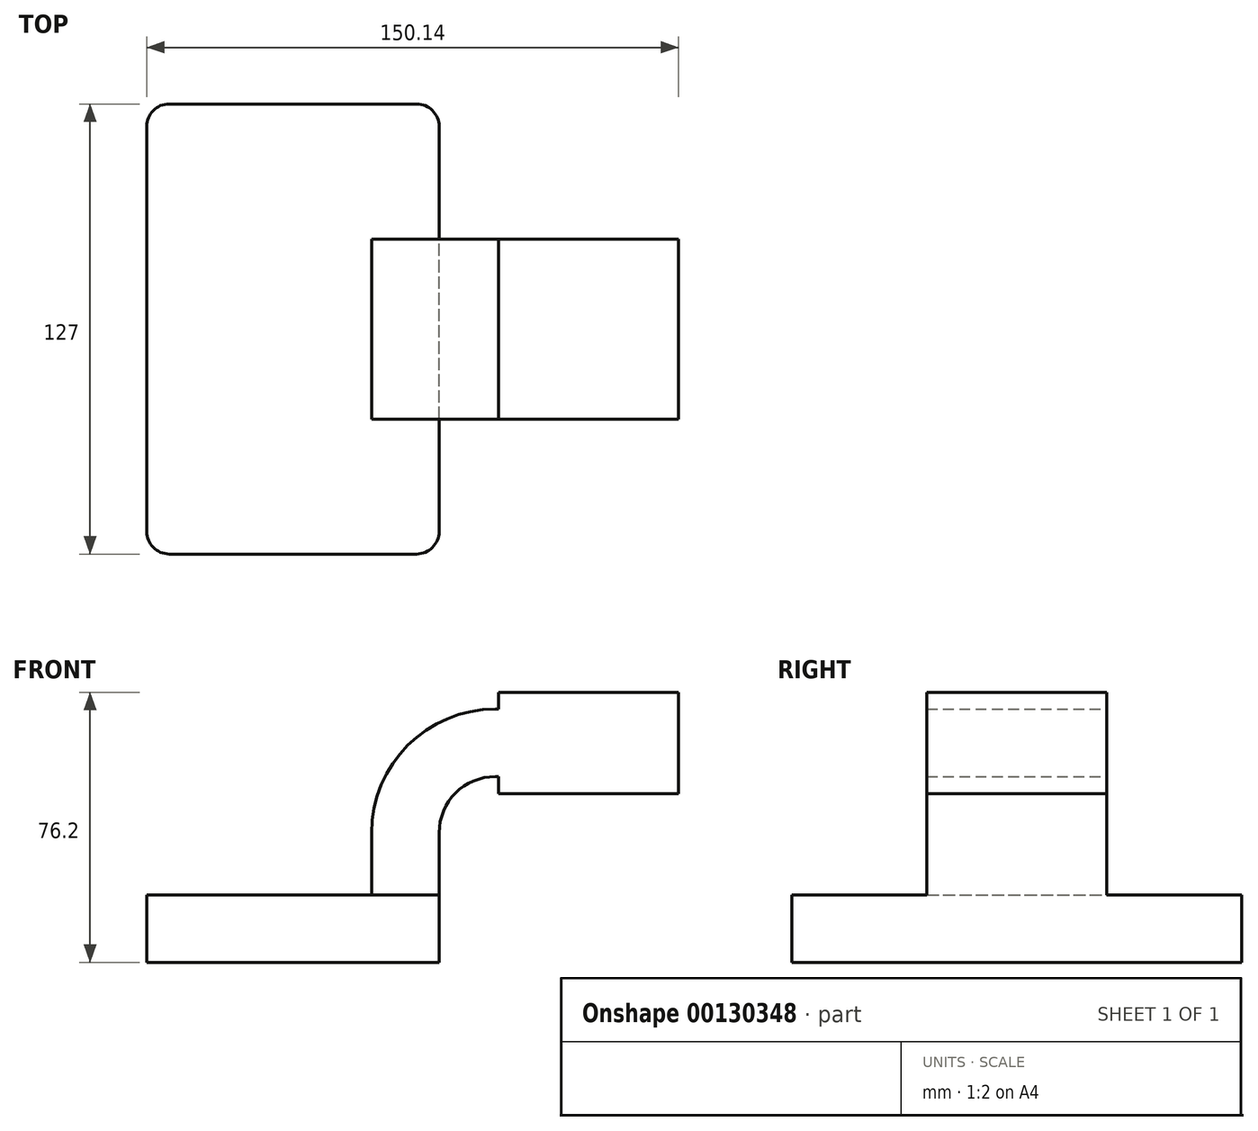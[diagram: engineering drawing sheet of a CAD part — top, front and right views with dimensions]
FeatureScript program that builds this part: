
annotation { "Feature Type Name" : "Feature", "Feature Type Description" : "" }
export const myFeature = defineFeature(function(context is Context, id is Id, definition is map)
    precondition{}
    {
        {
            var Q0;
            Q0=qCreatedBy(makeId("Front.planeOp"),FACE);
            var sketch = newSketch(context, id + "F0", { "sketchPlane" : qUnion([Q0])});
            skLineSegment(sketch, "E0.bottom", {"start": v(41.28, -9.52) * mm, "end": v(-41.28, -9.53) * mm});
            skLineSegment(sketch, "E0.top", {"start": v(41.28, 9.53) * mm, "end": v(-41.28, 9.53) * mm});
            skLineSegment(sketch, "E0.left", {"start": v(41.28, -9.52) * mm, "end": v(41.28, 9.53) * mm});
            skLineSegment(sketch, "E0.right", {"start": v(-41.28, -9.53) * mm, "end": v(-41.28, 9.53) * mm});
            skPoint(sketch, "E0.middle", {"position": v(0, 0) * mm});
            skLineSegment(sketch, "E1.bottom", {"start": v(108.87, 38.1) * mm, "end": v(58.07, 38.1) * mm});
            skLineSegment(sketch, "E1.top", {"start": v(108.87, 66.68) * mm, "end": v(58.07, 66.68) * mm});
            skLineSegment(sketch, "E1.left", {"start": v(108.87, 38.1) * mm, "end": v(108.87, 66.68) * mm});
            skLineSegment(sketch, "E1.right", {"start": v(58.07, 38.1) * mm, "end": v(58.07, 66.68) * mm});
            skPoint(sketch, "E1.middle", {"position": v(83.47, 52.39) * mm});
            skLineSegment(sketch, "E2", {"start": v(41.28, 9.53) * mm, "end": v(41.28, 27) * mm});
            skArc(sketch, "E3", {"start": v(41.27, 27) * mm, "mid": v(45.92, 38.23) * mm, "end": v(57.15, 42.88) * mm});
            skLineSegment(sketch, "E4", {"start": v(57.15, 42.88) * mm, "end": v(85.72, 42.88) * mm});
            skLineSegment(sketch, "E5.0", {"start": v(57.15, 61.93) * mm, "end": v(85.72, 61.93) * mm});
            skArc(sketch, "E5.1", {"start": v(22.23, 27) * mm, "mid": v(32.45, 51.7) * mm, "end": v(57.15, 61.93) * mm});
            skLineSegment(sketch, "E5.2", {"start": v(22.23, 9.53) * mm, "end": v(22.23, 27) * mm});
            skLineSegment(sketch, "E6", {"start": v(85.72, 42.88) * mm, "end": v(85.72, 66.68) * mm});
            skLineSegment(sketch, "E7", {"start": v(85.72, 42.88) * mm, "end": v(85.72, 38.1) * mm});
            skPoint(sketch, "E7.endSnap0", {"position": v(83.47, 38.1) * mm});
            skFitSpline(sketch, "E8", {"points": [v(-41.28, 9.53) * mm, v(57.15, 61.93) * mm], "startDerivative": vector(-1.56, 64.84) * mm, "endDerivative": vector(113.57, -0.62) * mm});
            skSolve(sketch);
        }
        {
            var Q0;
            Q0=makeQuery(id+"F0.imprint","IMPRINT",FACE,{"disambiguationData":[TD([[makeQuery(id+"F0.imprint","IMPRINT",EDGE,{"derivedFrom":sQuery(id+"F0.wireOp",EDGE,"E0.bottom")}),-1.0]])]});
            extrude(context, id + "F1", {"entities" : qUnion([Q0]), "endBound" : BoundingType.SYMMETRIC, "depth" : 127 * mm});
        }
        {
            var Q0;
            {var subQ1=sQuery(id+"F0.wireOp",EDGE,"E2");Q0=makeQuery(id+"F0.imprint","IMPRINT",FACE,{"disambiguationData":[TD([[makeQuery(id+"F0.imprint","IMPRINT",EDGE,{"derivedFrom":subQ1}),1.0]])]});}
            var Q1;
            {var subQ0=sQuery(id+"F0.wireOp",EDGE,"E4");var subQ1=sQuery(id+"F0.wireOp",EDGE,"E1.right");var subQ2=makeQuery(id+"F0.imprint","INTERSECT",VERTEX,{"derivedFrom":[subQ1,subQ0]});Q1=makeQuery(id+"F0.imprint","IMPRINT",FACE,{"disambiguationData":[TD([[makeQuery(id+"F0.imprint","IMPRINT",EDGE,{"disambiguationData":[TD([[subQ2,-1.0]])],"derivedFrom":subQ1}),-1.0]])]});}
            var Q2;
            {var subQ0=sQuery(id+"F0.wireOp",EDGE,"E1.left");Q2=makeQuery(id+"F0.imprint","IMPRINT",FACE,{"disambiguationData":[TD([[makeQuery(id+"F0.imprint","IMPRINT",EDGE,{"derivedFrom":subQ0}),1.0]])]});}
            var Q3;
            {var subQ0=sQuery(id+"F0.wireOp",EDGE,"E1.right");var subQ1=sQuery(id+"F0.wireOp",EDGE,"E1.top");var subQ2=makeQuery(id+"F0.imprint","INTERSECT",VERTEX,{"derivedFrom":[subQ1,subQ0]});Q3=makeQuery(id+"F0.imprint","IMPRINT",FACE,{"disambiguationData":[TD([[makeQuery(id+"F0.imprint","IMPRINT",EDGE,{"disambiguationData":[TD([[subQ2,1.0]])],"derivedFrom":subQ1}),1.0]])]});}
            var Q4;
            {var subQ3=sQuery(id+"F0.wireOp",EDGE,"E7");Q4=makeQuery(id+"F0.imprint","IMPRINT",FACE,{"disambiguationData":[TD([[makeQuery(id+"F0.imprint","IMPRINT",EDGE,{"derivedFrom":subQ3}),-1.0]])]});}
            extrude(context, id + "F2", {"entities" : qUnion([Q0, Q1, Q2, Q3, Q4]), "operationType" : NewBodyOperationType.ADD, "endBound" : BoundingType.SYMMETRIC, "depth" : 50.8 * mm});
        }
        {
            var Q0;
            Q0=makeQuery(id+"F0.imprint","IMPRINT",FACE,{"disambiguationData":[TD([[makeQuery(id+"F0.imprint","IMPRINT",EDGE,{"derivedFrom":sQuery(id+"F0.wireOp",EDGE,"E5.1")}),1.0]])]});
            extrude(context, id + "F3", {"entities" : qUnion([Q0]), "operationType" : NewBodyOperationType.ADD, "depth" : 19.05 * mm});
        }
        {
            var Q0;
            Q0=makeQuery(id+"F1.opExtrude","CAP_EDGE",EDGE,{"disambiguationData":[OSD([sQuery(id+"F0.wireOp",EDGE,"E0.left")])],"isStart":false});
            var Q1;
            Q1=makeQuery(id+"F1.opExtrude","CAP_EDGE",EDGE,{"disambiguationData":[OSD([sQuery(id+"F0.wireOp",EDGE,"E0.right")])],"isStart":false});
            fillet(context, id + "F4", {"entities" : qUnion([Q0, Q1]), "radius" : 6.35 * mm, "tangentPropagation" : true, "allowEdgeOverflow" : false});
        }
        {
            var Q0;
            Q0=makeQuery(id+"F1.opExtrude","CAP_EDGE",EDGE,{"disambiguationData":[OSD([sQuery(id+"F0.wireOp",EDGE,"E0.left")])],"isStart":true});
            var Q1;
            Q1=makeQuery(id+"F1.opExtrude","CAP_EDGE",EDGE,{"disambiguationData":[OSD([sQuery(id+"F0.wireOp",EDGE,"E0.right")])],"isStart":true});
            fillet(context, id + "F5", {"entities" : qUnion([Q0, Q1]), "radius" : 6.35 * mm, "tangentPropagation" : true, "allowEdgeOverflow" : false});
        }
    });
